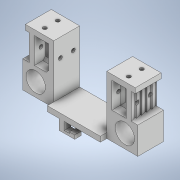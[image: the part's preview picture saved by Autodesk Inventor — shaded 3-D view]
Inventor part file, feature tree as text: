
AUTODESK INVENTOR PART (.ipt)
format: ipt  version: 2022 (Build 260153000, 153)  size: 333,312 bytes
history: native  units: mm
features: sketch x10, extrude x8, hole x2, other x1, chamfer x1
ambient origin geometry x8: Origin, YZ Plane, XZ Plane, XY Plane, X Axis, Y Axis, Z Axis, Center Point
bodies: Body1 (feature_tree), Body2 (feature_tree), Body3 (feature_tree)
feature tree (22):
  other  "Sólido1"
  extrude  "Extrusão1"  Depth=41.0mm
  extrude  "Extrusão2"  Depth=8.0mm
  extrude  "Extrusão3"  Depth=2.0mm
  extrude  "Extrusão4"  Depth=4.0mm
  hole  "Furo1"  [1 undecoded]
  extrude  "Extrusão6"  Depth=15.0mm TaperAngle=0.0deg
  extrude  "Extrusão7"  Depth=20.0mm
  extrude  "Extrusão8"  Depth=15.0mm
  hole  "Furo2"  [1 undecoded]
  extrude  "Extrusão10"  Depth=5.0mm
  chamfer  "Chanfro3"  Distance=5.0mm
  sketch  "Esboço1"  dims[d7=20.0mm d8=0.0mm d9=41.0mm]
  sketch  "Esboço2"  dims[d10=5.0mm d11=0.0mm d12=8.0mm]
  sketch  "Esboço3"  dims[d13=10.0mm d14=2.0mm]
  sketch  "Esboço5"  dims[d15=3.0mm d16=4.0mm]
  sketch  "Esboço7"  dims[d17=1.0mm d18=4.0mm]
  sketch  "Esboço8"  dims[d22=15.0mm d23=0.0mm d24=15.0mm d25=0.0mm]
  sketch  "Esboço10"  dims[d31=3.0mm d32=6.0mm d33=4.0mm d34=2.0mm d35=90.0deg d36=8.0mm d37=20.594885mm d38=20.0mm]
  sketch  "Esboço12"  dims[d39=20.0mm d40=15.0mm]
  sketch  "Esboço13"  dims[d41=15.0mm d42=10.0mm d43=0.0mm]
  sketch  "Esboço15"  dims[d44=5.0mm d45=5.0mm d46=5.0mm d47=5.0mm d49=10.0mm d50=10.0mm d51=10.0mm d52=10.0mm d53=4.0mm d54=0.0mm d55=4.0mm d56=0.0mm d60=4.0mm d61=75.0deg d62=100.0mm d64=4.0mm d65=10.0mm d67=10.0mm d71=3.0mm d72=6.0mm d73=4.0mm d74=2.0mm d75=90.0deg d76=8.0mm d77=20.594885mm d78=10.0mm d79=0.0mm d80=2.0mm d81=2.0mm d82=45.0deg d69=0.5mm d70=0.872665mm]
note: 2 required parameter values undecoded (feature->parameter linkage not recoverable at this tier; creation-order binding heuristic only, values carry confidence <= 0.55)
